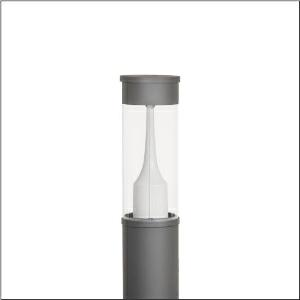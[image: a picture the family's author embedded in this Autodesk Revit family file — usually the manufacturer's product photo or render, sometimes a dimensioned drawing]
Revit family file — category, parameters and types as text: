
# Revit family: city-light_120_iq___p1_0a_5xa5285lf14h_baf3
name_source: partatom
category: Lighting Fixtures
units: mm (PartAtom-declared; Revit-internal decimal feet)

## family parameters
Cut with Voids When Loaded = No
Host = Face
Light Source = No
Part Type = Normal
Room Calculation Point = No
Round Connector Dimension = Use Diameter
Shared = No

## types (1)
- --- (1 x LED, 1510 lm, 10 W, 4000K)
    Apparent Load = 10 VA
    CIE Flux Codes = 32 61 90 93 100
    Color Rendering = 70
    Color Temperature = 4000K
    Default Elevation = 1800 mm
    Description = City-Light 120 iQ, bollard luminaire, Module 540 iQ-SR, primary light control with 3 zone facetted reflector, of plastic, silver coated, highly specular, structured, primary optical cover: cover, of PMMA, transparent, partly coated, light distribution: P1.0a, primary light characteristic: strongly asymmetric, LED, High Power LED, rated luminous flux: 1.510lm, luminous efficacy: 151lm/W, light colour: 740, colour temperature: 4000K, control gear: ECG iQ, control: presetting dimming logarithmic, Street-Remote, Auto-Match, Temp-Guard, Lumen-Switch, Night-Set, Smart-Wire, Light-Fading, Desk-Remote (wireless, voltage-free reading and setting of iQ features in the workshop via application-optimized NFC function/RFID function), optimised constant luminous flux control (CLO 2.0), with terminal, 6-pole, max. 2.5mm², mains connection: 230..240V, AC, 50/60Hz, start of lifetime: 10W, end of service life: 10W, reduction: 5W, luminaire housing, cylindrical, of extruded aluminium section, coated, Siteco® metallic grey (DB 702S), length: 1.200mm, diameter: 200mm, Module 540 iQ-SR, traffic white (RAL 9016), equipment: standard, protection rating (complete): IP54, insulation class (complete): insulation class II (safety insulation), certification: CE, ENEC, VDE, packaging unit: 1 piece

Light Distribution: P1.0a
    Height = 500 mm
    Lamp = 1 x LED
    Lamp Light Flux = 1510 lm
    Lamp Power = 10 W
    Lamp count = 1
    Length = 200 mm  [stored 0.656168 ft]
    Luminous efficacy = 151 lm/W
    Manufacturer = Siteco
    ModVariant = No
    Model = 5XA5285LF14H
    Mounting Place = Floor
    Mounting Type = Freestanding
    Number of Poles = 1
    OnlyDefault = Yes
    Power Factor = 1
    Product Name = City-Light 120 iQ | P1.0a
    Product group = bollard luminaire
    ProductGroupID = 1304
    Protection Class = Protection class II
    Protection Degree = IP 54
    RLX_Detail_Level = 1
    RLX_Emergency_Light_Flux = 0 lm
    RLX_Emergency_Type = 0
    RLX_Emergency_Type_DB = No
    RlxData = <blob elided: 52433 chars, md5=296780b3>
    Socket = socket
    Standby Power = 0 W
    System Light Flux = 1510 lm
    System Power = 10 W
    Type Comments = factory setting: luminous flux: 100 % | dim-lin: 254 | 401 mA
    Type Image = l_1006922.jpg
    URL = http://relux.com
    VarID = @adj_109739
    Voltage = 0 V
    Weight = 0.00 kg
    Width = 0 mm  [stored 0 ft]

note: [stored X ft] marks values corroborated as IEEE doubles in the binary element streams (Revit-internal decimal feet)

## geometry (parser evidence)
native form markers: Blend x4, Sweep x12
no freeform markers — native parametric forms only
